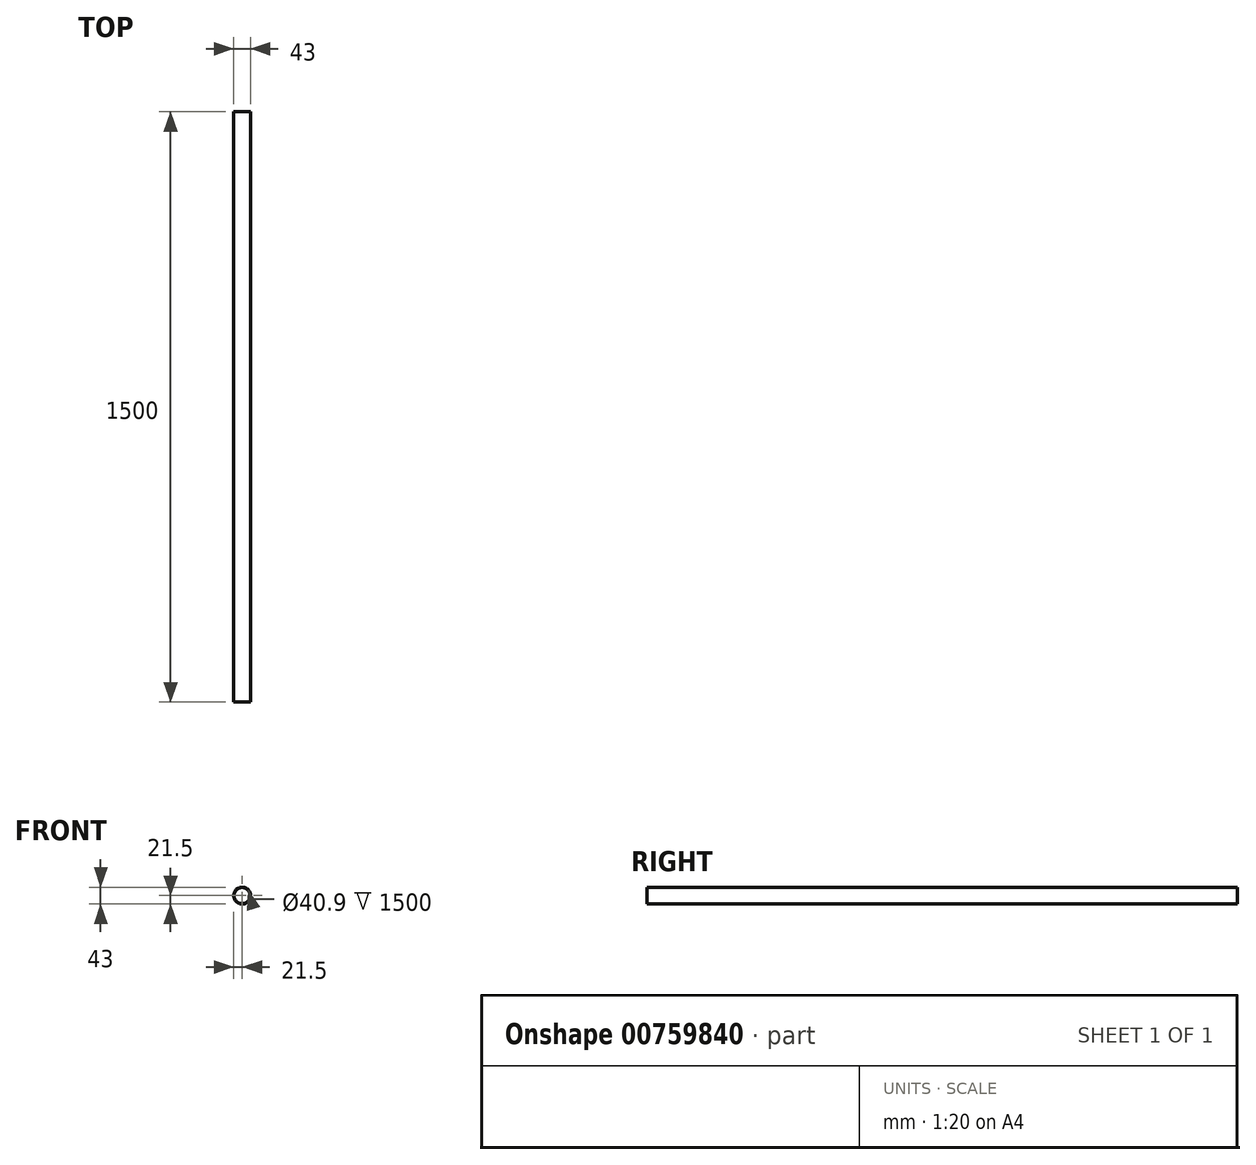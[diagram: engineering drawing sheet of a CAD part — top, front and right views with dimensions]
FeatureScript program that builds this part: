
annotation { "Feature Type Name" : "Feature", "Feature Type Description" : "" }
export const myFeature = defineFeature(function(context is Context, id is Id, definition is map)
    precondition{}
    {
        {
            assignVariable(context, id + "F0", {"name" : "LENGTH", "anyValue" : 1500});
        }
        {
            var Q0;
            Q0=qCreatedBy(makeId("Front.planeOp"),FACE);
            var sketch = newSketch(context, id + "F1", { "sketchPlane" : qUnion([Q0])});
            skCircle(sketch, "E0", {"center": v(0, 0) * mm, "radius": 20.45 * mm});
            skCircle(sketch, "E1", {"center": v(0, 0) * mm, "radius": 21.5 * mm});
            skSolve(sketch);
        }
        {
            var Q0;
            Q0=makeQuery(id+"F1.imprint","IMPRINT",FACE,{"disambiguationData":[TD([[makeQuery(id+"F1.imprint","IMPRINT",EDGE,{"derivedFrom":sQuery(id+"F1.wireOp",EDGE,"E0")}),-1.0]])]});
            extrude(context, id + "F2", {"entities" : qUnion([Q0]), "depth" : (getVariable(context, 'LENGTH')) * mm, "offsetDistance" : 25 * mm});
        }
    });
